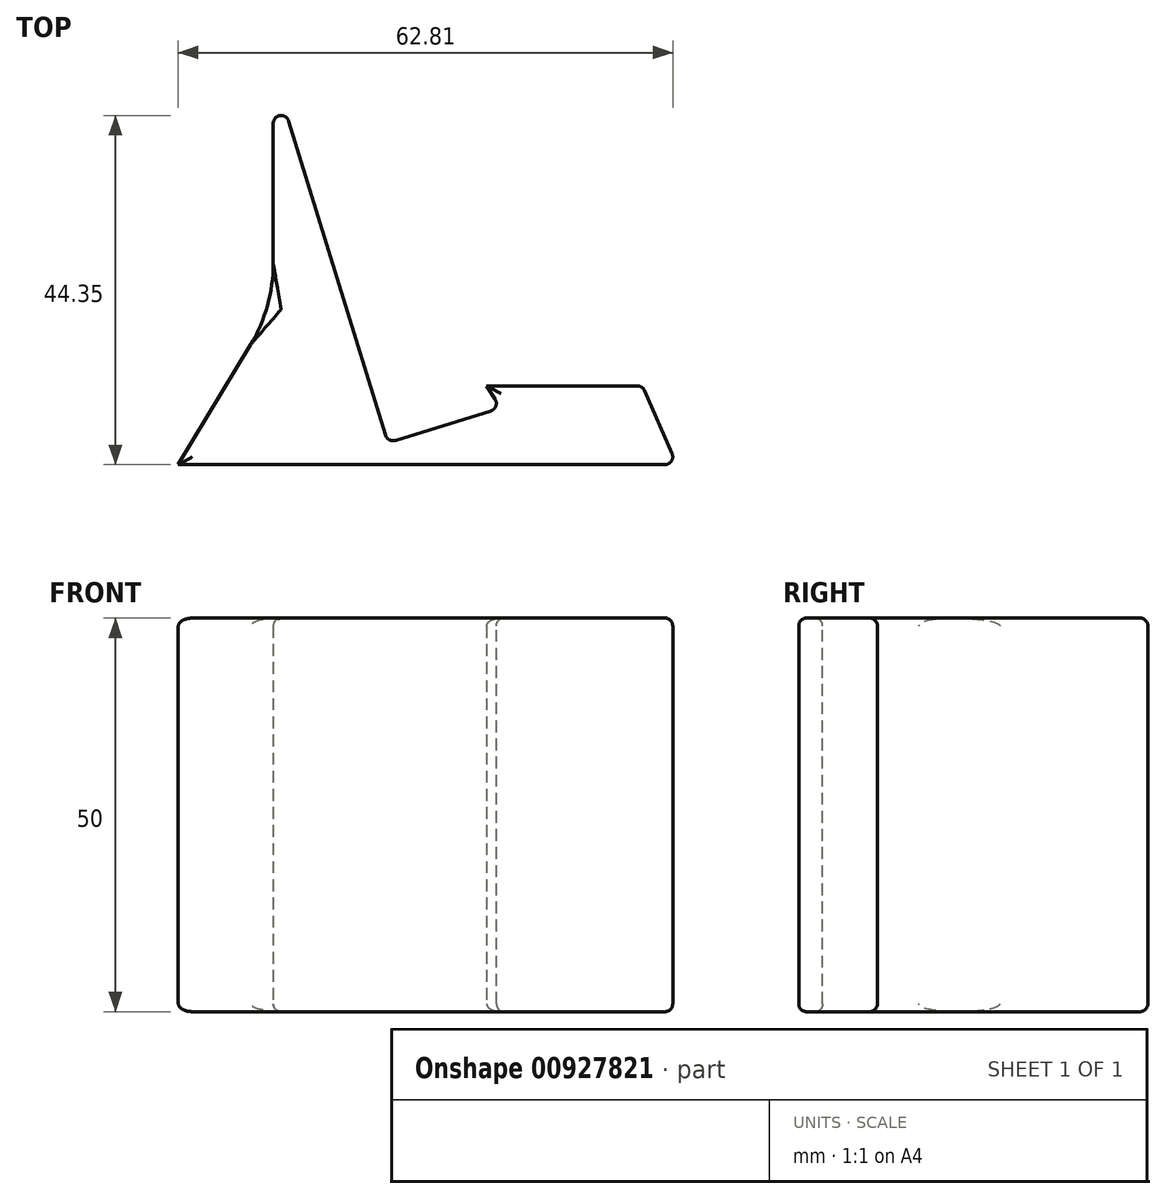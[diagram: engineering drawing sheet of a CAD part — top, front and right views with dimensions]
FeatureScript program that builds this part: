
annotation { "Feature Type Name" : "Feature", "Feature Type Description" : "" }
export const myFeature = defineFeature(function(context is Context, id is Id, definition is map)
    precondition{}
    {
        {
            var Q0;
            Q0=qCreatedBy(makeId("Top.planeOp"),FACE);
            var sketch = newSketch(context, id + "F0", { "sketchPlane" : qUnion([Q0])});
            skLineSegment(sketch, "E0", {"start": v(-95.82, 2.27) * mm, "end": v(-95.82, 12.27) * mm});
            skPoint(sketch, "E1.orphan", {"position": v(-54.08, -23.39) * mm});
            skLineSegment(sketch, "E2.0", {"start": v(-97.88, -17.72) * mm, "end": v(-44.54, -17.72) * mm});
            skLineSegment(sketch, "E3", {"start": v(-97.88, -17.72) * mm, "end": v(-107.88, -17.72) * mm});
            skPoint(sketch, "E4", {"position": v(-95.82, 12.27) * mm});
            skLineSegment(sketch, "E5", {"start": v(-95.82, 12.27) * mm, "end": v(-95.82, 32.27) * mm});
            skLineSegment(sketch, "E6", {"start": v(-107.88, -17.72) * mm, "end": v(-95.82, 2.27) * mm});
            skPoint(sketch, "E7.left.start.orphan", {"position": v(-95.82, -7.73) * mm});
            skLineSegment(sketch, "E8", {"start": v(-48.93, -7.72) * mm, "end": v(-68.72, -7.72) * mm});
            skLineSegment(sketch, "E9", {"start": v(-95.82, 32.27) * mm, "end": v(-83.5, -7.72) * mm});
            skLineSegment(sketch, "E10", {"start": v(-83.5, -7.72) * mm, "end": v(-81.27, -14.94) * mm});
            skLineSegment(sketch, "E11", {"start": v(-81.27, -14.94) * mm, "end": v(-66.94, -10.52) * mm});
            skLineSegment(sketch, "E12", {"start": v(-66.94, -10.52) * mm, "end": v(-68.72, -7.72) * mm});
            skLineSegment(sketch, "E13.trimOffspring", {"start": v(-83.5, -7.72) * mm, "end": v(-101.85, -7.72) * mm});
            skLineSegment(sketch, "E14.0", {"start": v(-46.81, -12.55) * mm, "end": v(-48.05, -9.73) * mm});
            skLineSegment(sketch, "E14.1", {"start": v(-44.54, -17.72) * mm, "end": v(-46.81, -12.55) * mm});
            skLineSegment(sketch, "E15", {"start": v(-48.05, -9.73) * mm, "end": v(-48.93, -7.72) * mm});
            skSolve(sketch);
        }
        {
            var Q0;
            {var subQ1=sQuery(id+"F0.wireOp",EDGE,"E0");Q0=makeQuery(id+"F0.imprint","IMPRINT",FACE,{"disambiguationData":[TD([[makeQuery(id+"F0.imprint","IMPRINT",EDGE,{"derivedFrom":subQ1}),-1.0]])]});}
            var Q1;
            Q1=makeQuery(id+"F0.imprint","IMPRINT",FACE,{"disambiguationData":[TD([[makeQuery(id+"F0.imprint","IMPRINT",EDGE,{"derivedFrom":sQuery(id+"F0.wireOp",EDGE,"E2.0")}),1.0]])]});
            extrude(context, id + "F1", {"entities" : qUnion([Q0, Q1]), "depth" : 50 * mm, "offsetDistance" : 25 * mm});
        }
        {
            var Q0;
            Q0=makeQuery(id+"F1.opExtrude","SWEPT_EDGE",EDGE,{"disambiguationData":[OSD([sQuery(id+"F0.wireOp",EDGE,"E5"),sQuery(id+"F0.wireOp",EDGE,"E9")])]});
            var Q1;
            Q1=makeQuery(id+"F1.opExtrude","SWEPT_EDGE",EDGE,{"disambiguationData":[OSD([sQuery(id+"F0.wireOp",EDGE,"E2.0"),sQuery(id+"F0.wireOp",EDGE,"E14.1")])]});
            var Q2;
            Q2=makeQuery(id+"F1.opExtrude","SWEPT_EDGE",EDGE,{"disambiguationData":[OSD([sQuery(id+"F0.wireOp",EDGE,"E8"),sQuery(id+"F0.wireOp",EDGE,"E15")])]});
            var Q3;
            Q3=makeQuery(id+"F1.opExtrude","SWEPT_EDGE",EDGE,{"disambiguationData":[OSD([sQuery(id+"F0.wireOp",EDGE,"E10"),sQuery(id+"F0.wireOp",EDGE,"E11")])]});
            var Q4;
            Q4=makeQuery(id+"F1.opExtrude","SWEPT_EDGE",EDGE,{"disambiguationData":[OSD([sQuery(id+"F0.wireOp",EDGE,"E11"),sQuery(id+"F0.wireOp",EDGE,"E12")])]});
            fillet(context, id + "F2", {"entities" : qUnion([Q0, Q1, Q2, Q3, Q4]), "radius" : 1 * mm, "tangentPropagation" : true, "allowEdgeOverflow" : false});
        }
        {
            var Q0;
            Q0=makeQuery(id+"F1.opExtrude","CAP_FACE",FACE,{"disambiguationData":[OSD([sQuery(id+"F0.wireOp",EDGE,"E0"),sQuery(id+"F0.wireOp",EDGE,"E2.0"),sQuery(id+"F0.wireOp",EDGE,"E3"),sQuery(id+"F0.wireOp",EDGE,"E5"),sQuery(id+"F0.wireOp",EDGE,"E6"),sQuery(id+"F0.wireOp",EDGE,"E8"),sQuery(id+"F0.wireOp",EDGE,"E9"),sQuery(id+"F0.wireOp",EDGE,"E10"),sQuery(id+"F0.wireOp",EDGE,"E11"),sQuery(id+"F0.wireOp",EDGE,"E12"),sQuery(id+"F0.wireOp",EDGE,"E14.0"),sQuery(id+"F0.wireOp",EDGE,"E14.1"),sQuery(id+"F0.wireOp",EDGE,"E15")])],"isStart":false});
            var Q1;
            Q1=makeQuery(id+"F1.opExtrude","CAP_FACE",FACE,{"disambiguationData":[OSD([sQuery(id+"F0.wireOp",EDGE,"E0"),sQuery(id+"F0.wireOp",EDGE,"E2.0"),sQuery(id+"F0.wireOp",EDGE,"E3"),sQuery(id+"F0.wireOp",EDGE,"E5"),sQuery(id+"F0.wireOp",EDGE,"E6"),sQuery(id+"F0.wireOp",EDGE,"E8"),sQuery(id+"F0.wireOp",EDGE,"E9"),sQuery(id+"F0.wireOp",EDGE,"E10"),sQuery(id+"F0.wireOp",EDGE,"E11"),sQuery(id+"F0.wireOp",EDGE,"E12"),sQuery(id+"F0.wireOp",EDGE,"E14.0"),sQuery(id+"F0.wireOp",EDGE,"E14.1"),sQuery(id+"F0.wireOp",EDGE,"E15")])],"isStart":true});
            fillet(context, id + "F3", {"entities" : qUnion([Q0, Q1]), "radius" : 1 * mm, "tangentPropagation" : true, "allowEdgeOverflow" : false});
        }
        {
            var Q0;
            Q0=makeQuery(id+"F1.opExtrude","SWEPT_EDGE",EDGE,{"disambiguationData":[OSD([sQuery(id+"F0.wireOp",EDGE,"E0"),sQuery(id+"F0.wireOp",EDGE,"E6")])]});
            fillet(context, id + "F4", {"entities" : qUnion([Q0]), "radius" : 20 * mm, "tangentPropagation" : true, "allowEdgeOverflow" : false});
        }
    });
